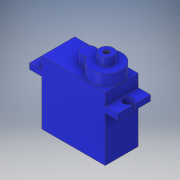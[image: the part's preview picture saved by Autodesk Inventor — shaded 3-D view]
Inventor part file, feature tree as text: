
AUTODESK INVENTOR PART (.ipt)
format: ipt  version: 2019.1 (Build 231200000, 200)  size: 218,624 bytes
history: native  units: in
note: dims shown in document units (in); Inventor stores cm internally (conversion verified against a paired STEP export)
features: extrude x7, sketch x7, thread x1
ambient origin geometry x8: Origin, YZ Plane, XZ Plane, XY Plane, X Axis, Y Axis, Z Axis, Center Point
bodies: Solid1 (feature_tree)
feature tree (15):
  extrude  "Extrusion1"  Depth=0.9055in
  sketch  "Sketch2"  dims[d2=0.9055in d3=0.0in d4=0.6496in]
  extrude  "Extrusion2"  Depth=0.6496in
  extrude  "Extrusion3"  Depth=0.1772in TaperAngle=0.0deg
  sketch  "Sketch4"  dims[d10=0.1772in d11=0.0in d12=0.1378in]
  extrude  "Extrusion5"  Depth=0.1772in
  extrude  "Extrusion6"  Depth=0.2362in
  extrude  "Extrusion7"  Depth=0.0886in
  extrude  "Extrusion8"  Depth=0.0394in
  thread  "Thread1"  [1 undecoded]
  sketch  "Sketch1"  dims[d0=0.4724in d1=0.9055in]
  sketch  "Sketch3"  dims[d7=0.0787in d8=0.1772in d9=0.0in]
  sketch  "Sketch6"  dims[d13=0.1378in d15=0.2362in]
  sketch  "Sketch7"  dims[d16=0.0886in d17=0.0886in]
  sketch  "Sketch8"  dims[d18=0.0886in d22=0.0394in d26=0.2165in d27=0.2165in d28=0.2165in d30=0.1772in d31=0.0in d32=0.4331in d33=0.1969in d34=0.2362in d35=0.2362in d36=0.2165in d37=0.4331in d38=0.2362in d39=0.2362in d40=0.1575in d41=0.0in d42=0.1969in d43=0.2362in d44=0.2362in d45=0.2165in d46=0.1181in d47=0.0in d48=0.0787in d49=0.1181in d50=0.0in d51=0.3937in d52=0.0in]
note: 1 required parameter value undecoded (feature->parameter linkage not recoverable at this tier; creation-order binding heuristic only, values carry confidence <= 0.55)
